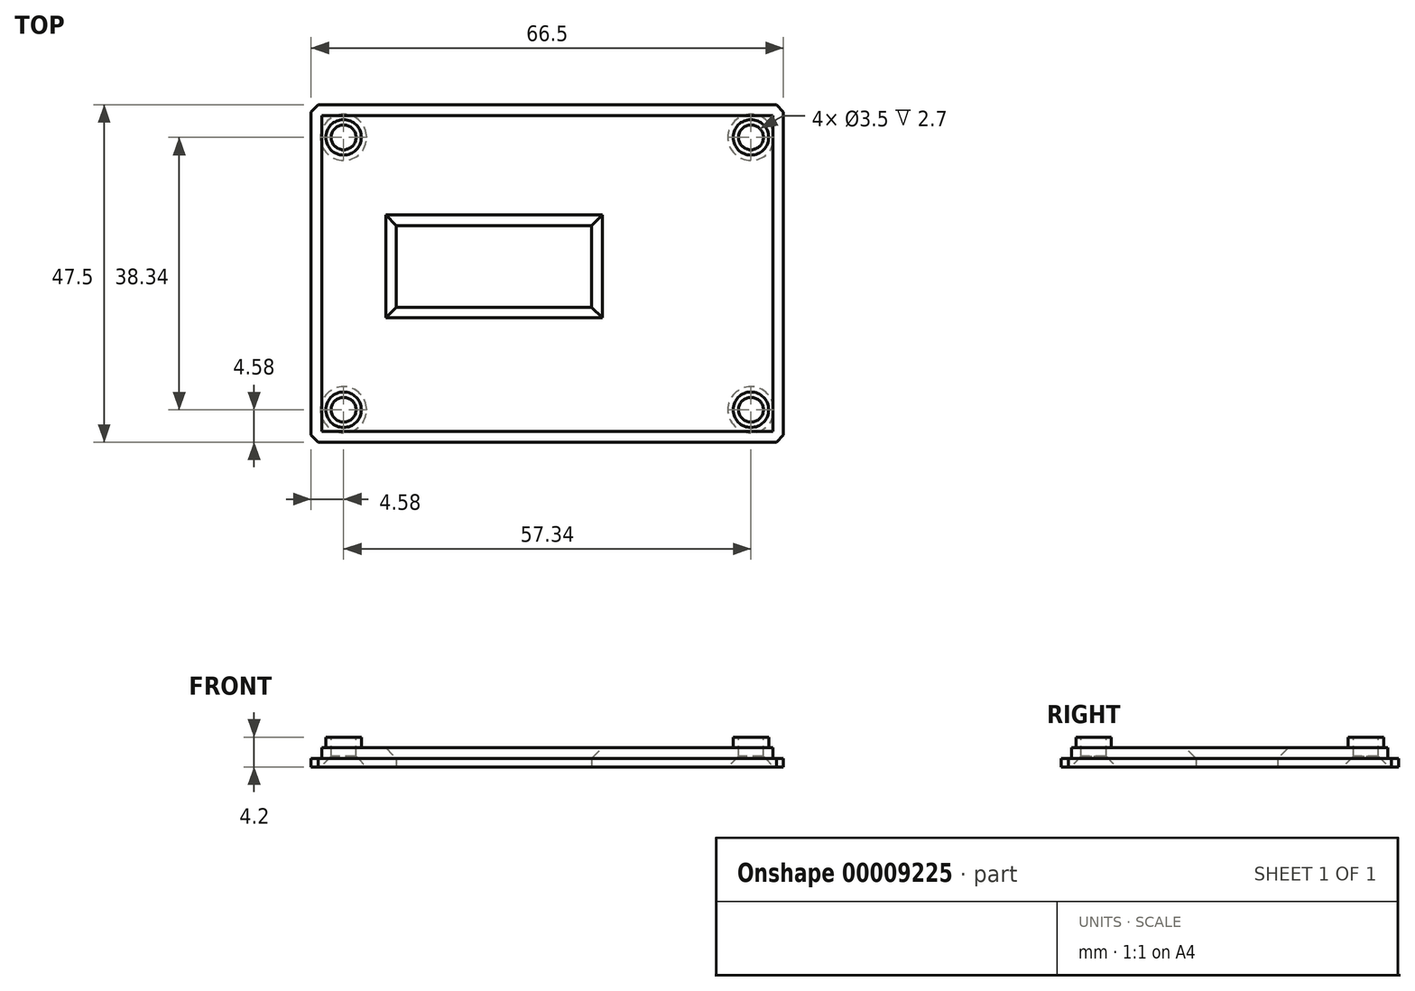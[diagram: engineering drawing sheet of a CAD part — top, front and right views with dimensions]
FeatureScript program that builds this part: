
annotation { "Feature Type Name" : "Feature", "Feature Type Description" : "" }
export const myFeature = defineFeature(function(context is Context, id is Id, definition is map)
    precondition{}
    {
        {
            var Q0;
            Q0=qCreatedBy(makeId("Top.planeOp"),FACE);
            var sketch = newSketch(context, id + "F0", { "sketchPlane" : qUnion([Q0])});
            skLineSegment(sketch, "E0.rect.bottom", {"start": v(33.25, 23.75) * mm, "end": v(-33.25, 23.75) * mm});
            skLineSegment(sketch, "E0.rect.top", {"start": v(33.25, -23.75) * mm, "end": v(-33.25, -23.75) * mm});
            skLineSegment(sketch, "E0.rect.left", {"start": v(33.25, 23.75) * mm, "end": v(33.25, -23.75) * mm});
            skLineSegment(sketch, "E0.rect.right", {"start": v(-33.25, 23.75) * mm, "end": v(-33.25, -23.75) * mm});
            skPoint(sketch, "E0.rect.middle", {"position": v(0, 0) * mm});
            skSolve(sketch);
        }
        {
            var Q0;
            Q0 = qSketchRegion(id + "F0", true);
            extrude(context, id + "F1", {"entities" : qUnion([Q0]), "depth" : 1.2 * mm});
        }
        {
            var Q0;
            Q0=makeQuery(id+"F1.opExtrude","CAP_FACE",FACE,{"disambiguationData":[OSD([sQuery(id+"F0.wireOp",EDGE,"E0.rect.bottom"),sQuery(id+"F0.wireOp",EDGE,"E0.rect.top"),sQuery(id+"F0.wireOp",EDGE,"E0.rect.left"),sQuery(id+"F0.wireOp",EDGE,"E0.rect.right")])],"isStart":false});
            var sketch = newSketch(context, id + "F2", { "sketchPlane" : qUnion([Q0])});
            skLineSegment(sketch, "E1.bottom", {"start": v(-31.75, 22.25) * mm, "end": v(31.75, 22.25) * mm});
            skLineSegment(sketch, "E1.top", {"start": v(-31.75, -22.25) * mm, "end": v(31.75, -22.25) * mm});
            skLineSegment(sketch, "E1.left", {"start": v(-31.75, 22.25) * mm, "end": v(-31.75, -22.25) * mm});
            skLineSegment(sketch, "E1.right", {"start": v(31.75, 22.25) * mm, "end": v(31.75, -22.25) * mm});
            skSolve(sketch);
        }
        {
            var Q0;
            Q0 = qSketchRegion(id + "F2", true);
            extrude(context, id + "F3", {"entities" : qUnion([Q0]), "operationType" : NewBodyOperationType.ADD, "depth" : 1.5 * mm});
        }
        {
            var Q0;
            Q0=makeQuery(id+"F3.opExtrude","CAP_FACE",FACE,{"disambiguationData":[OSD([sQuery(id+"F2.wireOp",EDGE,"E1.bottom"),sQuery(id+"F2.wireOp",EDGE,"E1.top"),sQuery(id+"F2.wireOp",EDGE,"E1.left"),sQuery(id+"F2.wireOp",EDGE,"E1.right")])],"isStart":false});
            var sketch = newSketch(context, id + "F4", { "sketchPlane" : qUnion([Q0])});
            skCircle(sketch, "E2", {"center": v(-28.67, -19.17) * mm, "radius": 2.5 * mm});
            skCircle(sketch, "E3.0.MirrorC", {"center": v(28.67, -19.17) * mm, "radius": 2.5 * mm});
            skCircle(sketch, "E4.0.MirrorC", {"center": v(-28.67, 19.17) * mm, "radius": 2.5 * mm});
            skCircle(sketch, "E5.0.MirrorC", {"center": v(28.67, 19.17) * mm, "radius": 2.5 * mm});
            skSolve(sketch);
        }
        {
            var Q0;
            Q0 = qSketchRegion(id + "F4", true);
            extrude(context, id + "F5", {"entities" : qUnion([Q0]), "operationType" : NewBodyOperationType.ADD, "depth" : 1.5 * mm});
        }
        {
            var Q0;
            Q0=makeQuery(id+"F5.opExtrude","CAP_FACE",FACE,{"disambiguationData":[OSD([sQuery(id+"F4.wireOp",EDGE,"E2")])],"isStart":false});
            var sketch = newSketch(context, id + "F6", { "sketchPlane" : qUnion([Q0])});
            skCircle(sketch, "E6", {"center": v(-28.67, -19.17) * mm, "radius": 1.75 * mm});
            skCircle(sketch, "E7.0.MirrorC", {"center": v(28.67, -19.17) * mm, "radius": 1.75 * mm});
            skCircle(sketch, "E8.0.MirrorC", {"center": v(-28.67, 19.17) * mm, "radius": 1.75 * mm});
            skCircle(sketch, "E9.0.MirrorC", {"center": v(28.67, 19.17) * mm, "radius": 1.75 * mm});
            skSolve(sketch);
        }
        {
            var Q0;
            Q0 = qSketchRegion(id + "F6", true);
            extrude(context, id + "F7", {"entities" : qUnion([Q0]), "operationType" : NewBodyOperationType.REMOVE, "endBound" : BoundingType.THROUGH_ALL, "oppositeDirection" : true, "depth" : 25 * mm});
        }
        {
            var Q0;
            Q0=makeQuery(id+"F1.opExtrude","CAP_FACE",FACE,{"disambiguationData":[OSD([sQuery(id+"F0.wireOp",EDGE,"E0.rect.bottom"),sQuery(id+"F0.wireOp",EDGE,"E0.rect.top"),sQuery(id+"F0.wireOp",EDGE,"E0.rect.left"),sQuery(id+"F0.wireOp",EDGE,"E0.rect.right")])],"isStart":true});
            var sketch = newSketch(context, id + "F8", { "sketchPlane" : qUnion([Q0])});
            skLineSegment(sketch, "E10.bottom", {"start": v(-21.25, 4.75) * mm, "end": v(6.25, 4.75) * mm});
            skLineSegment(sketch, "E10.top", {"start": v(-21.25, -6.75) * mm, "end": v(6.25, -6.75) * mm});
            skLineSegment(sketch, "E10.left", {"start": v(-21.25, 4.75) * mm, "end": v(-21.25, -6.75) * mm});
            skLineSegment(sketch, "E10.right", {"start": v(6.25, 4.75) * mm, "end": v(6.25, -6.75) * mm});
            skSolve(sketch);
        }
        {
            var Q0;
            Q0 = qSketchRegion(id + "F8", true);
            extrude(context, id + "F9", {"entities" : qUnion([Q0]), "operationType" : NewBodyOperationType.REMOVE, "endBound" : BoundingType.THROUGH_ALL, "oppositeDirection" : true, "depth" : 25 * mm});
        }
        {
            var Q0;
            Q0=makeQuery(id+"F7.boolean.opBoolean","INTERSECT",EDGE,{"derivedFrom":[makeQuery(id+"F1.opExtrude","CAP_FACE",FACE,{"disambiguationData":[OSD([sQuery(id+"F0.wireOp",EDGE,"E0.rect.bottom"),sQuery(id+"F0.wireOp",EDGE,"E0.rect.top"),sQuery(id+"F0.wireOp",EDGE,"E0.rect.left"),sQuery(id+"F0.wireOp",EDGE,"E0.rect.right")])],"isStart":true}),makeQuery(id+"F7.opExtrude","SWEPT_FACE",FACE,{"disambiguationData":[OSD([sQuery(id+"F6.wireOp",EDGE,"E6")])]})]});
            var Q1;
            Q1=makeQuery(id+"F7.boolean.opBoolean","INTERSECT",EDGE,{"derivedFrom":[makeQuery(id+"F1.opExtrude","CAP_FACE",FACE,{"disambiguationData":[OSD([sQuery(id+"F0.wireOp",EDGE,"E0.rect.bottom"),sQuery(id+"F0.wireOp",EDGE,"E0.rect.top"),sQuery(id+"F0.wireOp",EDGE,"E0.rect.left"),sQuery(id+"F0.wireOp",EDGE,"E0.rect.right")])],"isStart":true}),makeQuery(id+"F7.opExtrude","SWEPT_FACE",FACE,{"disambiguationData":[OSD([sQuery(id+"F6.wireOp",EDGE,"E7.0.MirrorC")])]})]});
            var Q2;
            Q2=makeQuery(id+"F7.boolean.opBoolean","INTERSECT",EDGE,{"derivedFrom":[makeQuery(id+"F1.opExtrude","CAP_FACE",FACE,{"disambiguationData":[OSD([sQuery(id+"F0.wireOp",EDGE,"E0.rect.bottom"),sQuery(id+"F0.wireOp",EDGE,"E0.rect.top"),sQuery(id+"F0.wireOp",EDGE,"E0.rect.left"),sQuery(id+"F0.wireOp",EDGE,"E0.rect.right")])],"isStart":true}),makeQuery(id+"F7.opExtrude","SWEPT_FACE",FACE,{"disambiguationData":[OSD([sQuery(id+"F6.wireOp",EDGE,"E9.0.MirrorC")])]})]});
            var Q3;
            Q3=makeQuery(id+"F7.boolean.opBoolean","INTERSECT",EDGE,{"derivedFrom":[makeQuery(id+"F1.opExtrude","CAP_FACE",FACE,{"disambiguationData":[OSD([sQuery(id+"F0.wireOp",EDGE,"E0.rect.bottom"),sQuery(id+"F0.wireOp",EDGE,"E0.rect.top"),sQuery(id+"F0.wireOp",EDGE,"E0.rect.left"),sQuery(id+"F0.wireOp",EDGE,"E0.rect.right")])],"isStart":true}),makeQuery(id+"F7.opExtrude","SWEPT_FACE",FACE,{"disambiguationData":[OSD([sQuery(id+"F6.wireOp",EDGE,"E8.0.MirrorC")])]})]});
            chamfer(context, id + "F10", {"entities" : qUnion([Q0, Q1, Q2, Q3]), "width" : 1.5 * mm, "tangentPropagation" : true});
        }
        {
            var Q0;
            Q0=makeQuery(id+"F1.opExtrude","SWEPT_EDGE",EDGE,{"disambiguationData":[OSD([sQuery(id+"F0.wireOp",EDGE,"E0.rect.top"),sQuery(id+"F0.wireOp",EDGE,"E0.rect.right")])]});
            var Q1;
            Q1=makeQuery(id+"F1.opExtrude","SWEPT_EDGE",EDGE,{"disambiguationData":[OSD([sQuery(id+"F0.wireOp",EDGE,"E0.rect.bottom"),sQuery(id+"F0.wireOp",EDGE,"E0.rect.right")])]});
            var Q2;
            Q2=makeQuery(id+"F1.opExtrude","SWEPT_EDGE",EDGE,{"disambiguationData":[OSD([sQuery(id+"F0.wireOp",EDGE,"E0.rect.bottom"),sQuery(id+"F0.wireOp",EDGE,"E0.rect.left")])]});
            var Q3;
            Q3=makeQuery(id+"F1.opExtrude","SWEPT_EDGE",EDGE,{"disambiguationData":[OSD([sQuery(id+"F0.wireOp",EDGE,"E0.rect.top"),sQuery(id+"F0.wireOp",EDGE,"E0.rect.left")])]});
            chamfer(context, id + "F11", {"entities" : qUnion([Q0, Q1, Q2, Q3]), "width" : 1 * mm, "tangentPropagation" : true});
        }
        {
            var Q0;
            Q0=makeQuery(id+"F9.boolean.opBoolean","INTERSECT",EDGE,{"derivedFrom":[makeQuery(id+"F3.opExtrude","CAP_FACE",FACE,{"disambiguationData":[OSD([sQuery(id+"F2.wireOp",EDGE,"E1.bottom"),sQuery(id+"F2.wireOp",EDGE,"E1.top"),sQuery(id+"F2.wireOp",EDGE,"E1.left"),sQuery(id+"F2.wireOp",EDGE,"E1.right")])],"isStart":false}),makeQuery(id+"F9.opExtrude","SWEPT_FACE",FACE,{"disambiguationData":[OSD([sQuery(id+"F8.wireOp",EDGE,"E10.top")])]})]});
            var Q1;
            Q1=makeQuery(id+"F9.boolean.opBoolean","INTERSECT",EDGE,{"derivedFrom":[makeQuery(id+"F3.opExtrude","CAP_FACE",FACE,{"disambiguationData":[OSD([sQuery(id+"F2.wireOp",EDGE,"E1.bottom"),sQuery(id+"F2.wireOp",EDGE,"E1.top"),sQuery(id+"F2.wireOp",EDGE,"E1.left"),sQuery(id+"F2.wireOp",EDGE,"E1.right")])],"isStart":false}),makeQuery(id+"F9.opExtrude","SWEPT_FACE",FACE,{"disambiguationData":[OSD([sQuery(id+"F8.wireOp",EDGE,"E10.right")])]})]});
            var Q2;
            Q2=makeQuery(id+"F9.boolean.opBoolean","INTERSECT",EDGE,{"derivedFrom":[makeQuery(id+"F3.opExtrude","CAP_FACE",FACE,{"disambiguationData":[OSD([sQuery(id+"F2.wireOp",EDGE,"E1.bottom"),sQuery(id+"F2.wireOp",EDGE,"E1.top"),sQuery(id+"F2.wireOp",EDGE,"E1.left"),sQuery(id+"F2.wireOp",EDGE,"E1.right")])],"isStart":false}),makeQuery(id+"F9.opExtrude","SWEPT_FACE",FACE,{"disambiguationData":[OSD([sQuery(id+"F8.wireOp",EDGE,"E10.bottom")])]})]});
            var Q3;
            Q3=makeQuery(id+"F9.boolean.opBoolean","INTERSECT",EDGE,{"derivedFrom":[makeQuery(id+"F3.opExtrude","CAP_FACE",FACE,{"disambiguationData":[OSD([sQuery(id+"F2.wireOp",EDGE,"E1.bottom"),sQuery(id+"F2.wireOp",EDGE,"E1.top"),sQuery(id+"F2.wireOp",EDGE,"E1.left"),sQuery(id+"F2.wireOp",EDGE,"E1.right")])],"isStart":false}),makeQuery(id+"F9.opExtrude","SWEPT_FACE",FACE,{"disambiguationData":[OSD([sQuery(id+"F8.wireOp",EDGE,"E10.left")])]})]});
            chamfer(context, id + "F12", {"entities" : qUnion([Q0, Q1, Q2, Q3]), "width" : 1.5 * mm, "tangentPropagation" : true});
        }
    });
